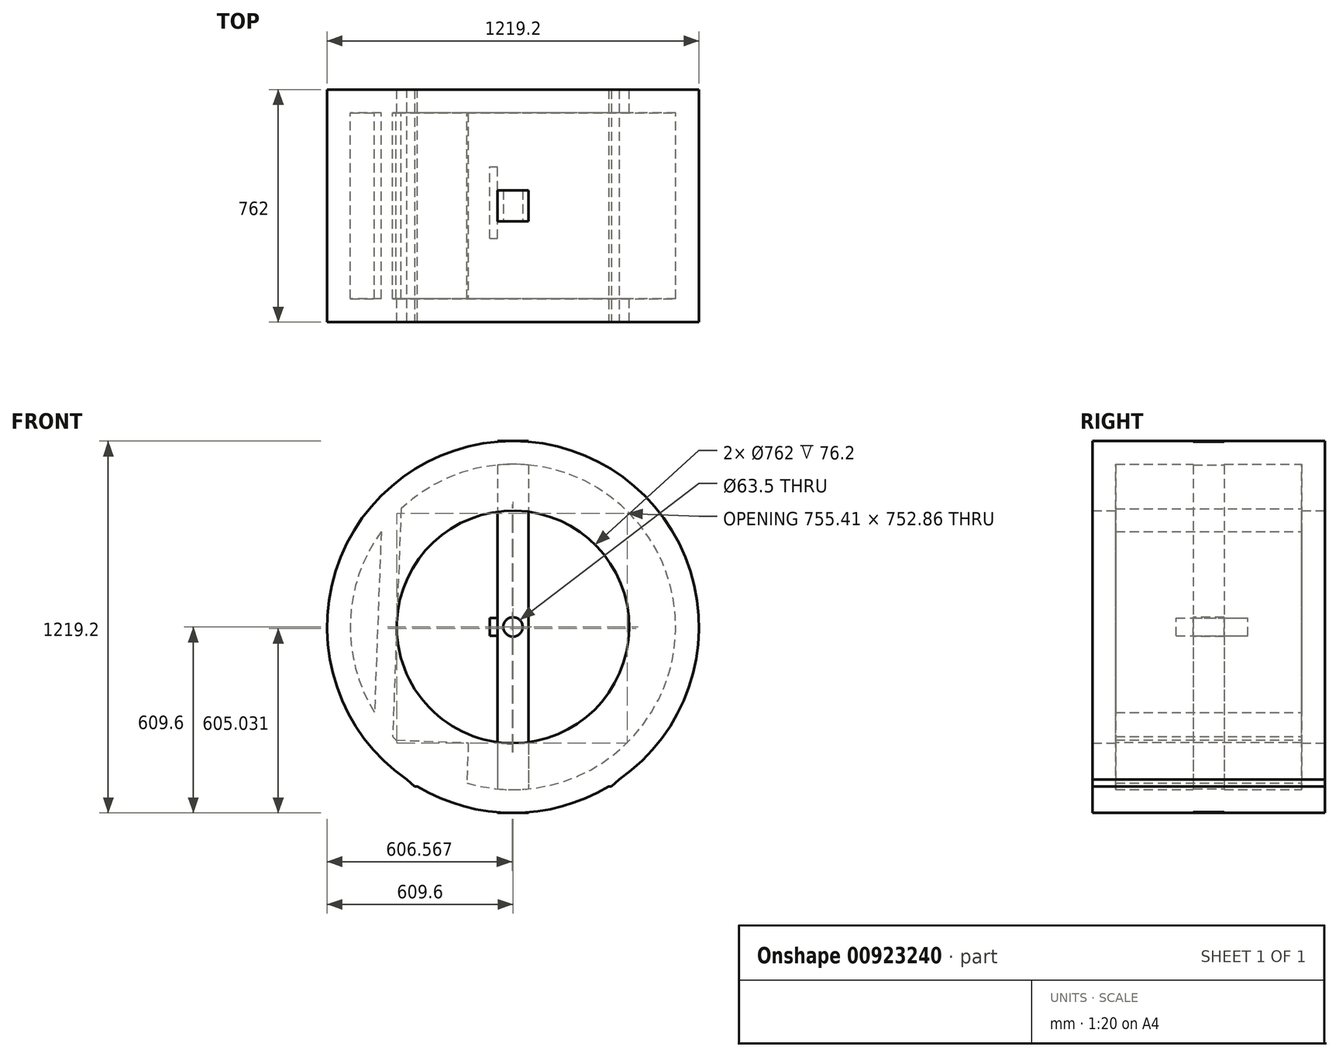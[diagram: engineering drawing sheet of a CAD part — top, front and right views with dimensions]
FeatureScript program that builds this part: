
annotation { "Feature Type Name" : "Feature", "Feature Type Description" : "" }
export const myFeature = defineFeature(function(context is Context, id is Id, definition is map)
    precondition{}
    {
        {
            var Q0;
            Q0=qCreatedBy(makeId("Front.planeOp"),FACE);
            var sketch = newSketch(context, id + "F0", { "sketchPlane" : qUnion([Q0])});
            skCircle(sketch, "E0", {"center": v(0, 0) * mm, "radius": 609.6 * mm});
            skCircle(sketch, "E1", {"center": v(0, 0) * mm, "radius": 381 * mm});
            skSolve(sketch);
        }
        {
            var Q0;
            Q0=makeQuery(id+"F0.imprint","IMPRINT",FACE,{"disambiguationData":[TD([[makeQuery(id+"F0.imprint","IMPRINT",EDGE,{"derivedFrom":sQuery(id+"F0.wireOp",EDGE,"E0")}),1.0]])]});
            extrude(context, id + "F1", {"entities" : qUnion([Q0]), "depth" : 762 * mm, "offsetDistance" : 25.4 * mm});
        }
        {
            var Q0;
            Q0=makeQuery(id+"F1.opExtrude","SWEPT_FACE",FACE,{"disambiguationData":[OSD([sQuery(id+"F0.wireOp",EDGE,"E1")])]});
            shell(context, id + "F2", {"entities" : qUnion([Q0]), "thickness" : 76.2 * mm});
        }
        {
            var Q0;
            Q0=makeQuery(id+"F1.opExtrude","CAP_FACE",FACE,{"disambiguationData":[OSD([sQuery(id+"F0.wireOp",EDGE,"E0"),sQuery(id+"F0.wireOp",EDGE,"E1")])],"isStart":false});
            var sketch = newSketch(context, id + "F3", { "sketchPlane" : qUnion([Q0])});
            skLineSegment(sketch, "E2", {"start": v(-365.38, 429.39) * mm, "end": v(-394.96, -370.47) * mm});
            skLineSegment(sketch, "E3", {"start": v(-394.96, -370.47) * mm, "end": v(-146.62, -379.66) * mm});
            skLineSegment(sketch, "E4", {"start": v(-146.62, -379.66) * mm, "end": v(-152.14, -528.75) * mm});
            skLineSegment(sketch, "E5", {"start": v(-152.14, -528.75) * mm, "end": v(-322.93, -522.44) * mm});
            skLineSegment(sketch, "E6", {"start": v(-365.38, 429.39) * mm, "end": v(-427.59, 431.69) * mm});
            skLineSegment(sketch, "E7", {"start": v(-427.59, 431.69) * mm, "end": v(-458.5, -404.2) * mm});
            skLineSegment(sketch, "E8", {"start": v(-458.5, -404.2) * mm, "end": v(-322.93, -522.44) * mm});
            skLineSegment(sketch, "E9", {"start": v(0, 607.19) * mm, "end": v(0, -610.74) * mm});
            skLineSegment(sketch, "E10.MirrorCS", {"start": v(146.62, -379.66) * mm, "end": v(152.14, -528.75) * mm});
            skLineSegment(sketch, "E11.MirrorCS", {"start": v(152.14, -528.75) * mm, "end": v(322.93, -522.44) * mm});
            skLineSegment(sketch, "E12.MirrorCS", {"start": v(458.5, -404.2) * mm, "end": v(322.93, -522.44) * mm});
            skLineSegment(sketch, "E13.MirrorCS", {"start": v(365.38, 429.39) * mm, "end": v(394.96, -370.47) * mm});
            skLineSegment(sketch, "E14.MirrorCS", {"start": v(427.59, 431.69) * mm, "end": v(458.5, -404.2) * mm});
            skLineSegment(sketch, "E15.MirrorCS", {"start": v(365.38, 429.39) * mm, "end": v(427.59, 431.69) * mm});
            skLineSegment(sketch, "E16.MirrorCS", {"start": v(394.96, -370.47) * mm, "end": v(146.62, -379.66) * mm});
            skSolve(sketch);
        }
        {
            var Q0;
            {var subQ0=sQuery(id+"F3.wireOp",EDGE,"E5");Q0=makeQuery(id+"F3.imprint","IMPRINT",FACE,{"disambiguationData":[TD([[makeQuery(id+"F3.imprint","IMPRINT",EDGE,{"derivedFrom":subQ0}),-1.0]])]});}
            var Q1;
            {var subQ0=sQuery(id+"F3.wireOp",EDGE,"E2");var subQ1=sQuery(id+"F0.wireOp",EDGE,"E1");var subQ2=makeQuery(id+"F3.imprint","INTERSECT",VERTEX,{"derivedFrom":[makeQuery(id+"F1.opExtrude","CAP_EDGE",EDGE,{"disambiguationData":[OSD([subQ1])],"isStart":false}),subQ0]});Q1=makeQuery(id+"F3.imprint","IMPRINT",FACE,{"disambiguationData":[TD([[makeQuery(id+"F3.imprint","IMPRINT",EDGE,{"disambiguationData":[TD([[subQ2,1.0]])],"derivedFrom":subQ0}),-1.0]])]});}
            var Q2;
            {var subQ0=sQuery(id+"F3.wireOp",EDGE,"E6");Q2=makeQuery(id+"F3.imprint","IMPRINT",FACE,{"disambiguationData":[TD([[makeQuery(id+"F3.imprint","IMPRINT",EDGE,{"derivedFrom":subQ0}),1.0]])]});}
            var Q3;
            {var subQ0=sQuery(id+"F3.wireOp",EDGE,"E15.MirrorCS");Q3=makeQuery(id+"F3.imprint","IMPRINT",FACE,{"disambiguationData":[TD([[makeQuery(id+"F3.imprint","IMPRINT",EDGE,{"derivedFrom":subQ0}),-1.0]])]});}
            var Q4;
            {var subQ9=sQuery(id+"F3.wireOp",EDGE,"E11.MirrorCS");Q4=makeQuery(id+"F3.imprint","IMPRINT",FACE,{"disambiguationData":[TD([[makeQuery(id+"F3.imprint","IMPRINT",EDGE,{"derivedFrom":subQ9}),1.0]])]});}
            extrude(context, id + "F4", {"entities" : qUnion([Q0, Q1, Q2, Q3, Q4]), "operationType" : NewBodyOperationType.ADD, "depth" : -762 * mm, "offsetDistance" : 25.4 * mm});
        }
        {
            var Q0;
            Q0=qCreatedBy(makeId("Top.planeOp"),FACE);
            var sketch = newSketch(context, id + "F5", { "sketchPlane" : qUnion([Q0])});
            skLineSegment(sketch, "E17.bottom", {"start": v(50.8, -330.2) * mm, "end": v(-50.8, -330.2) * mm});
            skLineSegment(sketch, "E17.top", {"start": v(50.8, -431.8) * mm, "end": v(-50.8, -431.8) * mm});
            skLineSegment(sketch, "E17.left", {"start": v(50.8, -330.2) * mm, "end": v(50.8, -431.8) * mm});
            skLineSegment(sketch, "E17.right", {"start": v(-50.8, -330.2) * mm, "end": v(-50.8, -431.8) * mm});
            skPoint(sketch, "E17.middle", {"position": v(0, -381) * mm});
            skLineSegment(sketch, "E18", {"start": v(-611.84, 0) * mm, "end": v(-611.84, -763.97) * mm});
            skSolve(sketch);
        }
        {
            var Q0;
            Q0=makeQuery(id+"F5.imprint","IMPRINT",FACE,{"disambiguationData":[TD([[makeQuery(id+"F5.imprint","IMPRINT",EDGE,{"derivedFrom":sQuery(id+"F5.wireOp",EDGE,"E17.bottom")}),1.0]])]});
            extrude(context, id + "F6", {"entities" : qUnion([Q0]), "operationType" : NewBodyOperationType.ADD, "depth" : 1219.2 * mm, "offsetDistance" : 25.4 * mm, "symmetric" : true});
        }
        {
            var Q0;
            Q0=makeQuery(id+"F6.boolean.opBoolean","SPLIT",FACE,{"disambiguationData":[TD([makeQuery(id+"F2.opShell","OFFSET_FACE",FACE,{"disambiguationData":[OSD([sQuery(id+"F0.wireOp",EDGE,"E0")])]}),makeQuery(id+"F6.opExtrude","SWEPT_FACE",FACE,{"disambiguationData":[OSD([sQuery(id+"F5.wireOp",EDGE,"E17.left")])]}),makeQuery(id+"F6.opExtrude","SWEPT_FACE",FACE,{"disambiguationData":[OSD([sQuery(id+"F5.wireOp",EDGE,"E17.right")])]})])],"derivedFrom":makeQuery(id+"F6.opExtrude","SWEPT_FACE",FACE,{"disambiguationData":[OSD([sQuery(id+"F5.wireOp",EDGE,"E17.top")])]})});
            var sketch = newSketch(context, id + "F7", { "sketchPlane" : qUnion([Q0])});
            skCircle(sketch, "E19", {"center": v(0, 0) * mm, "radius": 31.75 * mm});
            skSolve(sketch);
        }
        {
            var Q0;
            Q0=makeQuery(id+"F7.imprint","IMPRINT",FACE,{"disambiguationData":[TD([[makeQuery(id+"F7.imprint","IMPRINT",EDGE,{"derivedFrom":sQuery(id+"F7.wireOp",EDGE,"E19")}),1.0]])]});
            extrude(context, id + "F8", {"entities" : qUnion([Q0]), "operationType" : NewBodyOperationType.REMOVE, "oppositeDirection" : true, "depth" : 101.6 * mm, "offsetDistance" : 25.4 * mm});
        }
        {
            var Q0;
            Q0=makeQuery(id+"F6.boolean.opBoolean","SPLIT",FACE,{"disambiguationData":[TD([makeQuery(id+"F2.opShell","OFFSET_FACE",FACE,{"disambiguationData":[OSD([sQuery(id+"F0.wireOp",EDGE,"E0")])]})])],"derivedFrom":makeQuery(id+"F6.opExtrude","SWEPT_FACE",FACE,{"disambiguationData":[OSD([sQuery(id+"F5.wireOp",EDGE,"E17.right")])]})});
            var sketch = newSketch(context, id + "F9", { "sketchPlane" : qUnion([Q0])});
            skLineSegment(sketch, "E20.bottom", {"start": v(487.85, -29.34) * mm, "end": v(252.1, -29.34) * mm});
            skLineSegment(sketch, "E20.top", {"start": v(487.85, 29.34) * mm, "end": v(252.1, 29.34) * mm});
            skLineSegment(sketch, "E20.left", {"start": v(487.85, -29.34) * mm, "end": v(487.85, 29.34) * mm});
            skLineSegment(sketch, "E20.right", {"start": v(252.1, -29.34) * mm, "end": v(252.1, 29.34) * mm});
            skPoint(sketch, "E20.middle", {"position": v(369.98, 0) * mm});
            skSolve(sketch);
        }
        {
            var Q0;
            {var subQ0=sQuery(id+"F9.wireOp",EDGE,"E20.right");Q0=makeQuery(id+"F9.imprint","IMPRINT",FACE,{"disambiguationData":[TD([[makeQuery(id+"F9.imprint","IMPRINT",EDGE,{"derivedFrom":subQ0}),-1.0]])]});}
            var Q1;
            {var subQ0=sQuery(id+"F9.wireOp",EDGE,"E20.left");Q1=makeQuery(id+"F9.imprint","IMPRINT",FACE,{"disambiguationData":[TD([[makeQuery(id+"F9.imprint","IMPRINT",EDGE,{"derivedFrom":subQ0}),1.0]])]});}
            var Q2;
            {var subQ0=sQuery(id+"F9.wireOp",EDGE,"E20.bottom");var subQ1=makeQuery(id+"F2.opShell","OFFSET_FACE",FACE,{"disambiguationData":[OSD([sQuery(id+"F0.wireOp",EDGE,"E0")])]});var subQ2=sQuery(id+"F5.wireOp",EDGE,"E17.top");var subQ3=sQuery(id+"F5.wireOp",EDGE,"E17.right");var subQ5=makeQuery(id+"F6.boolean.opBoolean","SPLIT",EDGE,{"disambiguationData":[TD([subQ1])],"derivedFrom":makeQuery(id+"F6.opExtrude","SWEPT_EDGE",EDGE,{"disambiguationData":[OSD([subQ2,subQ3])]})});var subQ6=makeQuery(id+"F9.imprint","INTERSECT",VERTEX,{"derivedFrom":[subQ5,subQ0]});Q2=makeQuery(id+"F9.imprint","IMPRINT",FACE,{"disambiguationData":[TD([[makeQuery(id+"F9.imprint","IMPRINT",EDGE,{"disambiguationData":[TD([[subQ6,-1.0]])],"derivedFrom":subQ0}),-1.0]])]});}
            extrude(context, id + "F10", {"entities" : qUnion([Q0, Q1, Q2]), "operationType" : NewBodyOperationType.ADD, "depth" : 25.4 * mm, "offsetDistance" : 25.4 * mm});
        }
    });
